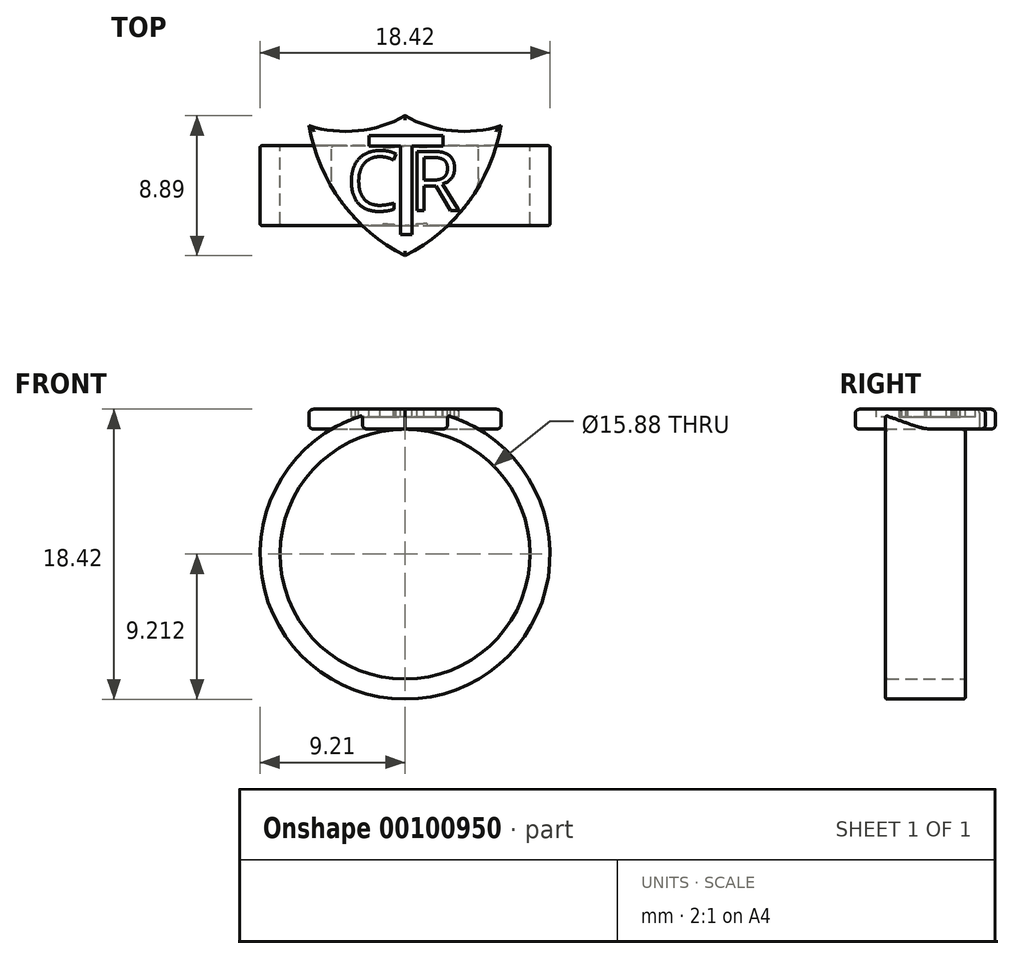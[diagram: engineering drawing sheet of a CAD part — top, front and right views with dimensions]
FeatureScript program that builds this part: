
annotation { "Feature Type Name" : "Feature", "Feature Type Description" : "" }
export const myFeature = defineFeature(function(context is Context, id is Id, definition is map)
    precondition{}
    {
        {
            var Q0;
            Q0=qCreatedBy(makeId("Top.planeOp"),FACE);
            var sketch = newSketch(context, id + "F0", { "sketchPlane" : qUnion([Q0])});
            skLineSegment(sketch, "E0", {"start": v(0, 0) * mm, "end": v(9.52, 0) * mm, "construction": true});
            skLineSegment(sketch, "E1", {"start": v(9.53, 0) * mm, "end": v(9.53, -8.9) * mm, "construction": true});
            skLineSegment(sketch, "E2", {"start": v(9.52, -8.89) * mm, "end": v(-9.52, -8.9) * mm, "construction": true});
            skLineSegment(sketch, "E3", {"start": v(-9.52, -8.9) * mm, "end": v(-9.52, 0) * mm, "construction": true});
            skLineSegment(sketch, "E4", {"start": v(-9.52, 0) * mm, "end": v(0, 0) * mm, "construction": true});
            skArc(sketch, "E5", {"start": v(-6.1, -0.63) * mm, "mid": v(-4.03, -5.49) * mm, "end": v(0, -8.89) * mm});
            skArc(sketch, "E6", {"start": v(-6.1, -0.64) * mm, "mid": v(-2.98, -0.96) * mm, "end": v(0, 0) * mm});
            skArc(sketch, "E7.MirrorCS", {"start": v(6.1, -0.64) * mm, "mid": v(2.98, -0.96) * mm, "end": v(0, 0) * mm});
            skArc(sketch, "E8.MirrorCS", {"start": v(6.1, -0.63) * mm, "mid": v(4.03, -5.49) * mm, "end": v(0, -8.89) * mm});
            skSolve(sketch);
        }
        {
            var Q0;
            Q0 = qSketchRegion(id + "F0", true);
            extrude(context, id + "F1", {"entities" : qUnion([Q0]), "depth" : 1.27 * mm});
        }
        {
            var Q0;
            Q0=qCreatedBy(makeId("Right.planeOp"),FACE);
            var sketch = newSketch(context, id + "F2", { "sketchPlane" : qUnion([Q0])});
            skLineSegment(sketch, "E9.bottom", {"start": v(-1.9, 0) * mm, "end": v(-6.98, 0) * mm});
            skLineSegment(sketch, "E9.top", {"start": v(-1.9, 1.27) * mm, "end": v(-6.98, 1.27) * mm});
            skLineSegment(sketch, "E9.left", {"start": v(-1.9, 1.27) * mm, "end": v(-1.9, 0) * mm});
            skLineSegment(sketch, "E9.right", {"start": v(-6.98, 1.27) * mm, "end": v(-6.98, 0) * mm});
            skLineSegment(sketch, "E10", {"start": v(0, 0) * mm, "end": v(-8.89, 0) * mm, "construction": true});
            skLineSegment(sketch, "E11", {"start": v(-4.44, 0) * mm, "end": v(-4.44, 3.33) * mm, "construction": true});
            skLineSegment(sketch, "E12", {"start": v(2.72, -7.94) * mm, "end": v(-10.6, -7.94) * mm, "construction": true});
            skLineSegment(sketch, "E13.0", {"start": v(-8.89, 1.27) * mm, "end": v(-8.89, 0) * mm, "construction": true});
            skSolve(sketch);
        }
        {
            var Q0;
            Q0 = qSketchRegion(id + "F2", true);
            var Q1;
            Q1=sQuery(id+"F2.wireOp",EDGE,"E12");
            revolve(context, id + "F3", {"operationType" : NewBodyOperationType.ADD, "entities" : qUnion([Q0]), "axis" : qUnion([Q1]), "revolveType" : RevolveType.FULL});
        }
        {
            var Q0;
            Q0=makeQuery(id+"F3.opRevolve","SWEPT_EDGE",EDGE,{"disambiguationData":[OSD([sQuery(id+"F2.wireOp",EDGE,"E9.top"),sQuery(id+"F2.wireOp",EDGE,"E9.right")])]});
            var Q1;
            Q1=makeQuery(id+"F3.opRevolve","SWEPT_EDGE",EDGE,{"disambiguationData":[OSD([sQuery(id+"F2.wireOp",EDGE,"E9.bottom"),sQuery(id+"F2.wireOp",EDGE,"E9.right")])]});
            var Q2;
            Q2=makeQuery(id+"F3.opRevolve","SWEPT_EDGE",EDGE,{"disambiguationData":[OSD([sQuery(id+"F2.wireOp",EDGE,"E9.top"),sQuery(id+"F2.wireOp",EDGE,"E9.left")])]});
            var Q3;
            Q3=makeQuery(id+"F3.opRevolve","SWEPT_EDGE",EDGE,{"disambiguationData":[OSD([sQuery(id+"F2.wireOp",EDGE,"E9.bottom"),sQuery(id+"F2.wireOp",EDGE,"E9.left")])]});
            fillet(context, id + "F4", {"entities" : qUnion([Q0, Q1, Q2, Q3]), "radius" : 0.13 * mm, "tangentPropagation" : true, "allowEdgeOverflow" : false});
        }
        {
            var Q0;
            Q0=makeQuery(id+"F1.opExtrude","CAP_FACE",FACE,{"disambiguationData":[OSD([sQuery(id+"F0.wireOp",EDGE,"dtAdijCY-2Pwo-jMmh-0q7I-SGrLHdXILtFh"),sQuery(id+"F0.wireOp",EDGE,"E5"),sQuery(id+"F0.wireOp",EDGE,"b53439b5-4433-4b26-adde-5d4ad1fb86ac0.MirrorCS"),sQuery(id+"F0.wireOp",EDGE,"ad21d0f8-95ba-4c56-aa77-77bde63a10fc0.MirrorCS")])],"isStart":false});
            var sketch = newSketch(context, id + "F5", { "sketchPlane" : qUnion([Q0])});
            skText(sketch, "E14", { "text": "T", "fontName": "OpenSans-Regular.ttf"});
            skText(sketch, "E15", { "text": "C\n", "fontName": "OpenSans-Regular.ttf"});
            skText(sketch, "E16", { "text": "R", "fontName": "OpenSans-Regular.ttf"});
            const initialGuessF5  = {"E14": [-0.00237, -0.00756, 1, 0, 0.00635], "E15": [-0.00373, -0.00603, 1, 0, 0.0038], "E16": [0.00024, -0.00603, 1, 0, 0.0038]};
            skSetInitialGuess(sketch, initialGuessF5);
            skSolve(sketch);
        }
        {
            var Q0;
            Q0 = qSketchRegion(id + "F5", true);
            extrude(context, id + "F6", {"entities" : qUnion([Q0]), "operationType" : NewBodyOperationType.REMOVE, "oppositeDirection" : true, "depth" : 0.5 * mm});
        }
        {
            var Q0;
            {var subQ0=sQuery(id+"F0.wireOp",EDGE,"ad21d0f8-95ba-4c56-aa77-77bde63a10fc0.MirrorCS");var subQ1=sQuery(id+"F0.wireOp",EDGE,"b53439b5-4433-4b26-adde-5d4ad1fb86ac0.MirrorCS");Q0=makeQuery(id+"F3.boolean.opBoolean","SPLIT",EDGE,{"disambiguationData":[TD([makeQuery(id+"F1.opExtrude","SWEPT_FACE",FACE,{"disambiguationData":[OSD([subQ1])]})])],"derivedFrom":makeQuery(id+"F1.opExtrude","CAP_EDGE",EDGE,{"disambiguationData":[OSD([subQ0])],"isStart":true})});}
            var Q1;
            {var subQ0=sQuery(id+"F0.wireOp",EDGE,"ad21d0f8-95ba-4c56-aa77-77bde63a10fc0.MirrorCS");var subQ1=sQuery(id+"F0.wireOp",EDGE,"E5");Q1=makeQuery(id+"F3.boolean.opBoolean","SPLIT",EDGE,{"disambiguationData":[TD([makeQuery(id+"F1.opExtrude","SWEPT_FACE",FACE,{"disambiguationData":[OSD([subQ1])]})])],"derivedFrom":makeQuery(id+"F1.opExtrude","CAP_EDGE",EDGE,{"disambiguationData":[OSD([subQ0])],"isStart":true})});}
            var Q2;
            {var subQ0=sQuery(id+"F0.wireOp",EDGE,"ad21d0f8-95ba-4c56-aa77-77bde63a10fc0.MirrorCS");var subQ1=sQuery(id+"F0.wireOp",EDGE,"E5");Q2=makeQuery(id+"F3.boolean.opBoolean","SPLIT",EDGE,{"disambiguationData":[TD([makeQuery(id+"F1.opExtrude","SWEPT_FACE",FACE,{"disambiguationData":[OSD([subQ0])]})])],"derivedFrom":makeQuery(id+"F1.opExtrude","CAP_EDGE",EDGE,{"disambiguationData":[OSD([subQ1])],"isStart":true})});}
            var Q3;
            {var subQ0=sQuery(id+"F0.wireOp",EDGE,"dtAdijCY-2Pwo-jMmh-0q7I-SGrLHdXILtFh");var subQ1=sQuery(id+"F0.wireOp",EDGE,"E5");Q3=makeQuery(id+"F3.boolean.opBoolean","SPLIT",EDGE,{"disambiguationData":[TD([makeQuery(id+"F1.opExtrude","SWEPT_FACE",FACE,{"disambiguationData":[OSD([subQ0])]})])],"derivedFrom":makeQuery(id+"F1.opExtrude","CAP_EDGE",EDGE,{"disambiguationData":[OSD([subQ1])],"isStart":true})});}
            var Q4;
            Q4=makeQuery(id+"F1.opExtrude","CAP_EDGE",EDGE,{"disambiguationData":[OSD([sQuery(id+"F0.wireOp",EDGE,"dtAdijCY-2Pwo-jMmh-0q7I-SGrLHdXILtFh")])],"isStart":true});
            var Q5;
            Q5=makeQuery(id+"F1.opExtrude","CAP_EDGE",EDGE,{"disambiguationData":[OSD([sQuery(id+"F0.wireOp",EDGE,"b53439b5-4433-4b26-adde-5d4ad1fb86ac0.MirrorCS")])],"isStart":true});
            var Q6;
            Q6=makeQuery(id+"F1.opExtrude","CAP_EDGE",EDGE,{"disambiguationData":[OSD([sQuery(id+"F0.wireOp",EDGE,"dtAdijCY-2Pwo-jMmh-0q7I-SGrLHdXILtFh")])],"isStart":false});
            var Q7;
            Q7=makeQuery(id+"F1.opExtrude","CAP_EDGE",EDGE,{"disambiguationData":[OSD([sQuery(id+"F0.wireOp",EDGE,"E5")])],"isStart":false});
            var Q8;
            Q8=makeQuery(id+"F1.opExtrude","CAP_EDGE",EDGE,{"disambiguationData":[OSD([sQuery(id+"F0.wireOp",EDGE,"ad21d0f8-95ba-4c56-aa77-77bde63a10fc0.MirrorCS")])],"isStart":false});
            var Q9;
            Q9=makeQuery(id+"F1.opExtrude","CAP_EDGE",EDGE,{"disambiguationData":[OSD([sQuery(id+"F0.wireOp",EDGE,"b53439b5-4433-4b26-adde-5d4ad1fb86ac0.MirrorCS")])],"isStart":false});
            var Q10;
            Q10=makeQuery(id+"F1.opExtrude","CAP_EDGE",EDGE,{"disambiguationData":[OSD([sQuery(id+"F0.wireOp",EDGE,"E6")])],"isStart":false});
            var Q11;
            Q11=makeQuery(id+"F1.opExtrude","CAP_EDGE",EDGE,{"disambiguationData":[OSD([sQuery(id+"F0.wireOp",EDGE,"E7.MirrorCS")])],"isStart":false});
            var Q12;
            Q12=makeQuery(id+"F1.opExtrude","CAP_EDGE",EDGE,{"disambiguationData":[OSD([sQuery(id+"F0.wireOp",EDGE,"E8.MirrorCS")])],"isStart":false});
            var Q13;
            {var subQ0=sQuery(id+"F0.wireOp",EDGE,"E8.MirrorCS");var subQ1=sQuery(id+"F0.wireOp",EDGE,"E7.MirrorCS");Q13=makeQuery(id+"F3.boolean.opBoolean","SPLIT",EDGE,{"disambiguationData":[TD([makeQuery(id+"F1.opExtrude","SWEPT_FACE",FACE,{"disambiguationData":[OSD([subQ1])]})])],"derivedFrom":makeQuery(id+"F1.opExtrude","CAP_EDGE",EDGE,{"disambiguationData":[OSD([subQ0])],"isStart":true})});}
            var Q14;
            {var subQ0=sQuery(id+"F0.wireOp",EDGE,"E5");var subQ1=sQuery(id+"F0.wireOp",EDGE,"E8.MirrorCS");Q14=makeQuery(id+"F3.boolean.opBoolean","SPLIT",EDGE,{"disambiguationData":[TD([makeQuery(id+"F1.opExtrude","SWEPT_FACE",FACE,{"disambiguationData":[OSD([subQ0])]})])],"derivedFrom":makeQuery(id+"F1.opExtrude","CAP_EDGE",EDGE,{"disambiguationData":[OSD([subQ1])],"isStart":true})});}
            var Q15;
            {var subQ0=sQuery(id+"F0.wireOp",EDGE,"E5");var subQ1=sQuery(id+"F0.wireOp",EDGE,"E8.MirrorCS");Q15=makeQuery(id+"F3.boolean.opBoolean","SPLIT",EDGE,{"disambiguationData":[TD([makeQuery(id+"F1.opExtrude","SWEPT_FACE",FACE,{"disambiguationData":[OSD([subQ1])]})])],"derivedFrom":makeQuery(id+"F1.opExtrude","CAP_EDGE",EDGE,{"disambiguationData":[OSD([subQ0])],"isStart":true})});}
            var Q16;
            {var subQ0=sQuery(id+"F0.wireOp",EDGE,"E5");var subQ1=sQuery(id+"F0.wireOp",EDGE,"E6");Q16=makeQuery(id+"F3.boolean.opBoolean","SPLIT",EDGE,{"disambiguationData":[TD([makeQuery(id+"F1.opExtrude","SWEPT_FACE",FACE,{"disambiguationData":[OSD([subQ1])]})])],"derivedFrom":makeQuery(id+"F1.opExtrude","CAP_EDGE",EDGE,{"disambiguationData":[OSD([subQ0])],"isStart":true})});}
            var Q17;
            Q17=makeQuery(id+"F1.opExtrude","CAP_EDGE",EDGE,{"disambiguationData":[OSD([sQuery(id+"F0.wireOp",EDGE,"E6")])],"isStart":true});
            var Q18;
            Q18=makeQuery(id+"F1.opExtrude","CAP_EDGE",EDGE,{"disambiguationData":[OSD([sQuery(id+"F0.wireOp",EDGE,"E7.MirrorCS")])],"isStart":true});
            fillet(context, id + "F7", {"entities" : qUnion([Q0, Q1, Q2, Q3, Q4, Q5, Q6, Q7, Q8, Q9, Q10, Q11, Q12, Q13, Q14, Q15, Q16, Q17, Q18]), "radius" : 0.25 * mm, "tangentPropagation" : true, "allowEdgeOverflow" : false});
        }
    });
